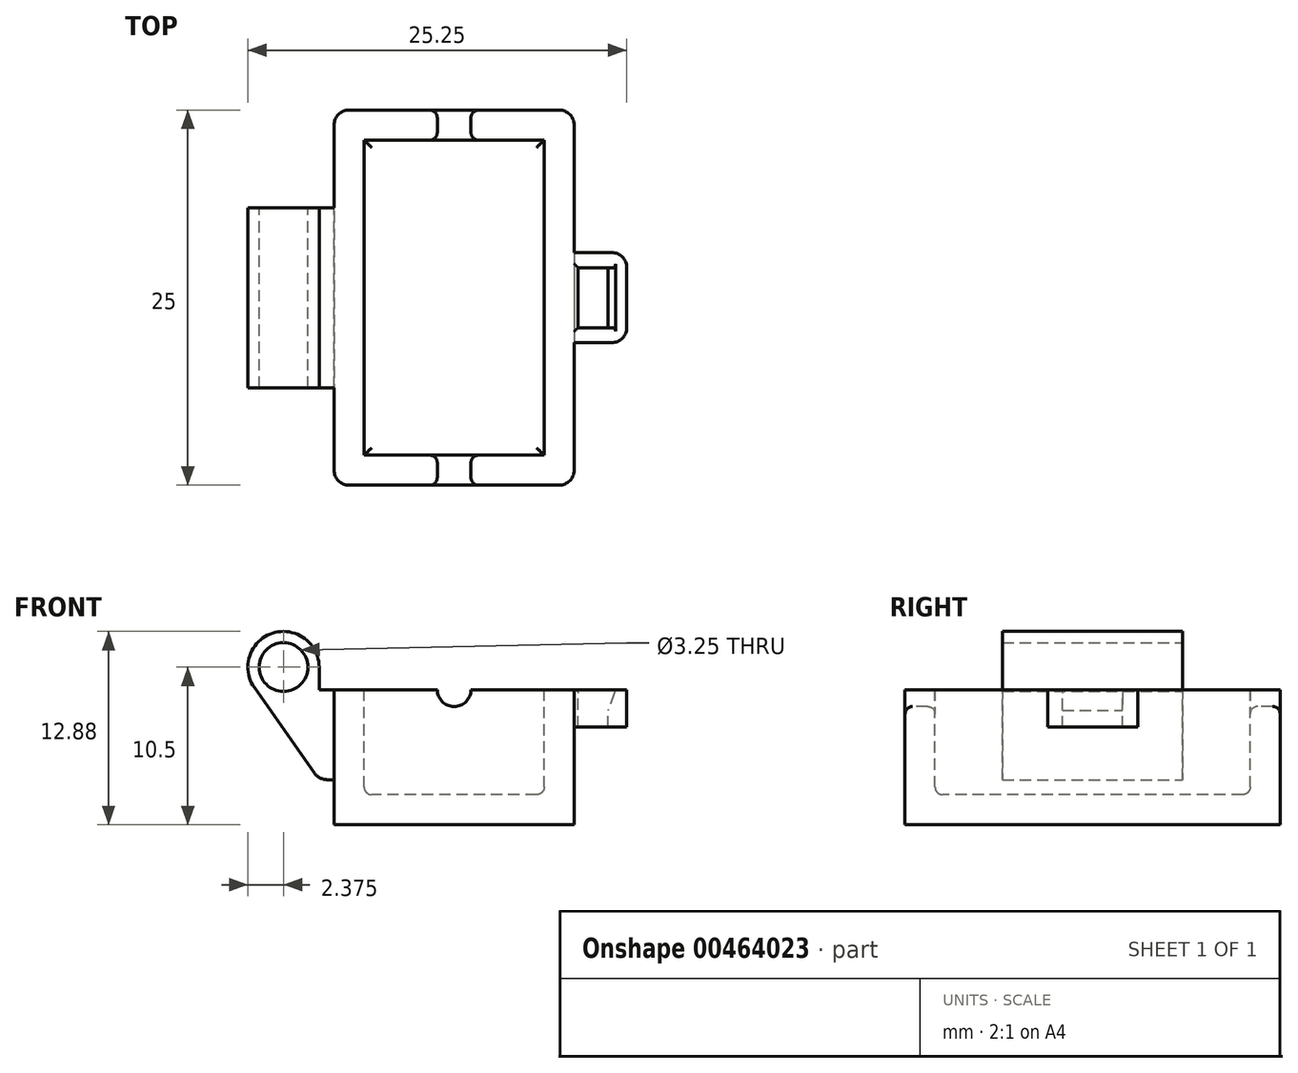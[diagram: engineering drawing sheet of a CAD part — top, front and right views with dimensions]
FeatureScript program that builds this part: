
annotation { "Feature Type Name" : "Feature", "Feature Type Description" : "" }
export const myFeature = defineFeature(function(context is Context, id is Id, definition is map)
    precondition{}
    {
        {
            var Q0;
            Q0=qCreatedBy(makeId("Top.planeOp"),FACE);
            var sketch = newSketch(context, id + "F0", { "sketchPlane" : qUnion([Q0])});
            skLineSegment(sketch, "E0.bottom", {"start": v(8, 12.5) * mm, "end": v(-8, 12.5) * mm});
            skLineSegment(sketch, "E0.top", {"start": v(8, -12.5) * mm, "end": v(-8, -12.5) * mm});
            skLineSegment(sketch, "E0.left", {"start": v(8, 12.5) * mm, "end": v(8, -12.5) * mm});
            skLineSegment(sketch, "E0.right", {"start": v(-8, 12.5) * mm, "end": v(-8, -12.5) * mm});
            skPoint(sketch, "E0.middle", {"position": v(0, 0) * mm});
            skSolve(sketch);
        }
        {
            var Q0;
            Q0 = qSketchRegion(id + "F0", true);
            extrude(context, id + "F1", {"entities" : qUnion([Q0]), "oppositeDirection" : true, "depth" : 9 * mm});
        }
        {
            var Q0;
            Q0=makeQuery(id+"F1.opExtrude","CAP_FACE",FACE,{"disambiguationData":[OSD([sQuery(id+"F0.wireOp",EDGE,"E0.bottom"),sQuery(id+"F0.wireOp",EDGE,"E0.top"),sQuery(id+"F0.wireOp",EDGE,"E0.left"),sQuery(id+"F0.wireOp",EDGE,"E0.right")])],"isStart":true});
            shell(context, id + "F2", {"entities" : qUnion([Q0]), "thickness" : 2 * mm});
        }
        {
            var Q0;
            Q0=qCreatedBy(makeId("Front.planeOp"),FACE);
            var sketch = newSketch(context, id + "F3", { "sketchPlane" : qUnion([Q0])});
            skLineSegment(sketch, "E1", {"start": v(-13.32, 0.13) * mm, "end": v(-9, -6) * mm});
            skArc(sketch, "E2", {"start": v(-9, 1.5) * mm, "mid": v(-12.1, 3.76) * mm, "end": v(-13.32, 0.13) * mm});
            skLineSegment(sketch, "E3", {"start": v(-9, 1.5) * mm, "end": v(-9, 0) * mm});
            skLineSegment(sketch, "E4", {"start": v(-9, 0) * mm, "end": v(-8, 0) * mm});
            skLineSegment(sketch, "E5.0", {"start": v(-8, -6) * mm, "end": v(-8, 0) * mm});
            skLineSegment(sketch, "E6", {"start": v(-9, -6) * mm, "end": v(-8, -6) * mm});
            skPoint(sketch, "E7.orphan", {"position": v(-8, -9) * mm});
            skSolve(sketch);
        }
        {
            var Q0;
            Q0 = qSketchRegion(id + "F3", true);
            extrude(context, id + "F4", {"entities" : qUnion([Q0]), "operationType" : NewBodyOperationType.ADD, "endBound" : BoundingType.SYMMETRIC, "depth" : 12 * mm});
        }
        {
            var Q0;
            Q0=makeQuery(id+"F4.opExtrude","CAP_FACE",FACE,{"disambiguationData":[OSD([sQuery(id+"F3.wireOp",EDGE,"uH9xqNTA-Io9C-N20J-ZzZ9-npMpiWseRlYH"),sQuery(id+"F3.wireOp",EDGE,"l0RrsI6B-aDfr-OfvM-JG3k-yMFCeRe5ejhv"),sQuery(id+"F3.wireOp",EDGE,"E1"),sQuery(id+"F3.wireOp",EDGE,"81e93450-e998-4614-a5fd-c4c0534a458d.0"),sQuery(id+"F3.wireOp",EDGE,"b74dccb4-ed0e-4af8-89a9-468f63bd8629.0")])],"isStart":true});
            var sketch = newSketch(context, id + "F5", { "sketchPlane" : qUnion([Q0])});
            skCircle(sketch, "E8", {"center": v(11.38, 1.5) * mm, "radius": 1.63 * mm});
            skSolve(sketch);
        }
        {
            var Q0;
            Q0 = qSketchRegion(id + "F5", true);
            extrude(context, id + "F6", {"entities" : qUnion([Q0]), "operationType" : NewBodyOperationType.REMOVE, "oppositeDirection" : true, "depth" : 25 * mm});
        }
        {
            var Q0;
            Q0=qCreatedBy(makeId("Front.planeOp"),FACE);
            var sketch = newSketch(context, id + "F7", { "sketchPlane" : qUnion([Q0])});
            skCircle(sketch, "E9", {"center": v(0, 0) * mm, "radius": 1.13 * mm});
            skSolve(sketch);
        }
        {
            var Q0;
            Q0 = qSketchRegion(id + "F7", true);
            extrude(context, id + "F8", {"entities" : qUnion([Q0]), "operationType" : NewBodyOperationType.REMOVE, "oppositeDirection" : true, "depth" : 25 * mm, "hasSecondDirection" : true, "secondDirectionOppositeDirection" : false, "secondDirectionDepth" : 25 * mm});
        }
        {
            var Q0;
            Q0=makeQuery(id+"F4.opExtrude","SWEPT_EDGE",EDGE,{"disambiguationData":[OSD([sQuery(id+"F3.wireOp",EDGE,"E1"),sQuery(id+"F3.wireOp",EDGE,"81e93450-e998-4614-a5fd-c4c0534a458d.0")])]});
            fillet(context, id + "F9", {"entities" : qUnion([Q0]), "radius" : 1 * mm, "tangentPropagation" : true, "allowEdgeOverflow" : false});
        }
        {
            var Q0;
            Q0=makeQuery(id+"F1.opExtrude","SWEPT_FACE",FACE,{"disambiguationData":[OSD([sQuery(id+"F0.wireOp",EDGE,"E0.left")])]});
            var sketch = newSketch(context, id + "F10", { "sketchPlane" : qUnion([Q0])});
            skLineSegment(sketch, "E10.bottom", {"start": v(1, -1.75) * mm, "end": v(-1, -1.75) * mm});
            skLineSegment(sketch, "E10.top", {"start": v(1, -0.75) * mm, "end": v(-1, -0.75) * mm});
            skLineSegment(sketch, "E10.left", {"start": v(1, -1.75) * mm, "end": v(1, -0.75) * mm});
            skLineSegment(sketch, "E10.right", {"start": v(-1, -1.75) * mm, "end": v(-1, -0.75) * mm});
            skPoint(sketch, "E10.middle", {"position": v(0, -1.25) * mm});
            skSolve(sketch);
        }
        {
            var Q0;
            {var subQ0=sQuery(id+"F0.wireOp",EDGE,"E0.left");var subQ1=sQuery(id+"F0.wireOp",EDGE,"E0.top");var subQ2=sQuery(id+"F0.wireOp",EDGE,"E0.bottom");Q0=makeQuery(id+"F8.boolean.opBoolean","SPLIT",FACE,{"disambiguationData":[TD([makeQuery(id+"F1.opExtrude","SWEPT_FACE",FACE,{"disambiguationData":[OSD([subQ0])]})])],"derivedFrom":makeQuery(id+"F1.opExtrude","CAP_FACE",FACE,{"disambiguationData":[OSD([subQ2,subQ1,subQ0,sQuery(id+"F0.wireOp",EDGE,"E0.right")])],"isStart":true})});}
            var sketch = newSketch(context, id + "F11", { "sketchPlane" : qUnion([Q0])});
            skLineSegment(sketch, "E11.bottom", {"start": v(8, 3) * mm, "end": v(11.5, 3) * mm});
            skLineSegment(sketch, "E11.top", {"start": v(8, -3) * mm, "end": v(11.5, -3) * mm});
            skLineSegment(sketch, "E11.left", {"start": v(8, 3) * mm, "end": v(8, -3) * mm});
            skLineSegment(sketch, "E11.right", {"start": v(11.5, 3) * mm, "end": v(11.5, -3) * mm});
            skLineSegment(sketch, "E12.bottom", {"start": v(8.25, 2) * mm, "end": v(10.25, 2) * mm});
            skLineSegment(sketch, "E12.top", {"start": v(8.25, -2) * mm, "end": v(10.25, -2) * mm});
            skLineSegment(sketch, "E12.left", {"start": v(8.25, 2) * mm, "end": v(8.25, -2) * mm});
            skLineSegment(sketch, "E12.right", {"start": v(10.25, 2) * mm, "end": v(10.25, -2) * mm});
            skSolve(sketch);
        }
        {
            var Q0;
            Q0 = qSketchRegion(id + "F11", true);
            extrude(context, id + "F12", {"entities" : qUnion([Q0]), "operationType" : NewBodyOperationType.ADD, "oppositeDirection" : true, "depth" : 2.5 * mm});
        }
        {
            var Q0;
            Q0=makeQuery(id+"F12.opExtrude","SWEPT_EDGE",EDGE,{"disambiguationData":[OSD([sQuery(id+"F11.wireOp",EDGE,"E11.top"),sQuery(id+"F11.wireOp",EDGE,"E11.right")])]});
            var Q1;
            Q1=makeQuery(id+"F12.opExtrude","SWEPT_EDGE",EDGE,{"disambiguationData":[OSD([sQuery(id+"F0.wireOp",EDGE,"E0.left"),sQuery(id+"F11.wireOp",EDGE,"E11.top"),sQuery(id+"F11.wireOp",EDGE,"E11.left")])]});
            var Q2;
            Q2=makeQuery(id+"F12.opExtrude","SWEPT_EDGE",EDGE,{"disambiguationData":[OSD([sQuery(id+"F11.wireOp",EDGE,"E11.bottom"),sQuery(id+"F11.wireOp",EDGE,"E11.right")])]});
            var Q3;
            Q3=makeQuery(id+"F12.opExtrude","SWEPT_EDGE",EDGE,{"disambiguationData":[OSD([sQuery(id+"F0.wireOp",EDGE,"E0.left"),sQuery(id+"F11.wireOp",EDGE,"E11.bottom"),sQuery(id+"F11.wireOp",EDGE,"E11.left")])]});
            fillet(context, id + "F13", {"entities" : qUnion([Q0, Q1, Q2, Q3]), "radius" : 1 * mm, "tangentPropagation" : true, "allowEdgeOverflow" : false});
        }
        {
            var Q0;
            Q0=makeQuery(id+"F12.opExtrude","CAP_EDGE",EDGE,{"disambiguationData":[OSD([sQuery(id+"F11.wireOp",EDGE,"E12.bottom")])],"isStart":true});
            var Q1;
            Q1=makeQuery(id+"F12.opExtrude","CAP_EDGE",EDGE,{"disambiguationData":[OSD([sQuery(id+"F11.wireOp",EDGE,"E12.left")])],"isStart":true});
            var Q2;
            Q2=makeQuery(id+"F12.opExtrude","CAP_EDGE",EDGE,{"disambiguationData":[OSD([sQuery(id+"F11.wireOp",EDGE,"E12.top")])],"isStart":true});
            fillet(context, id + "F14", {"entities" : qUnion([Q0, Q1, Q2]), "radius" : .25 * mm, "tangentPropagation" : true, "allowEdgeOverflow" : false});
        }
        {
            var Q0;
            Q0=makeQuery(id+"F12.opExtrude","CAP_EDGE",EDGE,{"disambiguationData":[OSD([sQuery(id+"F11.wireOp",EDGE,"E12.right")])],"isStart":true});
            chamfer(context, id + "F15", {"entities" : qUnion([Q0]), "chamferType" : ChamferType.OFFSET_ANGLE, "width" : .5 * mm, "oppositeDirection" : false, "angle" : 70 * degree, "tangentPropagation" : true});
        }
        {
            var Q0;
            Q0=makeQuery(id+"F8.boolean.opBoolean","INTERSECT",EDGE,{"derivedFrom":[makeQuery(id+"F1.opExtrude","SWEPT_FACE",FACE,{"disambiguationData":[OSD([sQuery(id+"F0.wireOp",EDGE,"E0.bottom")])]}),makeQuery(id+"F8.opExtrude","SWEPT_FACE",FACE,{"disambiguationData":[OSD([sQuery(id+"F7.wireOp",EDGE,"E9")])]})]});
            var Q1;
            Q1=makeQuery(id+"F8.boolean.opBoolean","INTERSECT",EDGE,{"derivedFrom":[makeQuery(id+"F1.opExtrude","SWEPT_FACE",FACE,{"disambiguationData":[OSD([sQuery(id+"F0.wireOp",EDGE,"E0.top")])]}),makeQuery(id+"F8.opExtrude","SWEPT_FACE",FACE,{"disambiguationData":[OSD([sQuery(id+"F7.wireOp",EDGE,"E9")])]})]});
            fillet(context, id + "F16", {"entities" : qUnion([Q0, Q1]), "radius" : .5 * mm, "tangentPropagation" : true, "allowEdgeOverflow" : false});
        }
        {
            var Q0;
            Q0=makeQuery(id+"F8.boolean.opBoolean","INTERSECT",EDGE,{"derivedFrom":[makeQuery(id+"F2.opShell","OFFSET_FACE",FACE,{"disambiguationData":[OSD([sQuery(id+"F0.wireOp",EDGE,"E0.bottom")])]}),makeQuery(id+"F8.opExtrude","SWEPT_FACE",FACE,{"disambiguationData":[OSD([sQuery(id+"F7.wireOp",EDGE,"E9")])]})]});
            var Q1;
            {var subQ0=sQuery(id+"F0.wireOp",EDGE,"E0.bottom");Q1=makeQuery(id+"F2.opShell","OFFSET_EDGE",EDGE,{"disambiguationData":[OSD([subQ0]),TDD([makeQuery(id+"F1.opExtrude","CAP_EDGE",EDGE,{"disambiguationData":[OSD([subQ0])],"isStart":false})])]});}
            var Q2;
            {var subQ0=sQuery(id+"F0.wireOp",EDGE,"E0.top");Q2=makeQuery(id+"F2.opShell","OFFSET_EDGE",EDGE,{"disambiguationData":[OSD([subQ0]),TDD([makeQuery(id+"F1.opExtrude","CAP_EDGE",EDGE,{"disambiguationData":[OSD([subQ0])],"isStart":false})])]});}
            var Q3;
            {var subQ0=sQuery(id+"F0.wireOp",EDGE,"E0.left");Q3=makeQuery(id+"F2.opShell","OFFSET_EDGE",EDGE,{"disambiguationData":[OSD([subQ0]),TDD([makeQuery(id+"F1.opExtrude","CAP_EDGE",EDGE,{"disambiguationData":[OSD([subQ0])],"isStart":false})])]});}
            var Q4;
            Q4=makeQuery(id+"F8.boolean.opBoolean","INTERSECT",EDGE,{"derivedFrom":[makeQuery(id+"F2.opShell","OFFSET_FACE",FACE,{"disambiguationData":[OSD([sQuery(id+"F0.wireOp",EDGE,"E0.top")])]}),makeQuery(id+"F8.opExtrude","SWEPT_FACE",FACE,{"disambiguationData":[OSD([sQuery(id+"F7.wireOp",EDGE,"E9")])]})]});
            var Q5;
            {var subQ0=sQuery(id+"F0.wireOp",EDGE,"E0.right");Q5=makeQuery(id+"F2.opShell","OFFSET_EDGE",EDGE,{"disambiguationData":[OSD([subQ0]),TDD([makeQuery(id+"F1.opExtrude","CAP_EDGE",EDGE,{"disambiguationData":[OSD([subQ0])],"isStart":false})])]});}
            fillet(context, id + "F17", {"entities" : qUnion([Q0, Q1, Q2, Q3, Q4, Q5]), "radius" : .5 * mm, "tangentPropagation" : true, "allowEdgeOverflow" : false});
        }
        {
            var Q0;
            Q0=makeQuery(id+"F1.opExtrude","SWEPT_EDGE",EDGE,{"disambiguationData":[OSD([sQuery(id+"F0.wireOp",EDGE,"E0.bottom"),sQuery(id+"F0.wireOp",EDGE,"E0.left")])]});
            var Q1;
            Q1=makeQuery(id+"F1.opExtrude","SWEPT_EDGE",EDGE,{"disambiguationData":[OSD([sQuery(id+"F0.wireOp",EDGE,"E0.bottom"),sQuery(id+"F0.wireOp",EDGE,"E0.right")])]});
            var Q2;
            Q2=makeQuery(id+"F1.opExtrude","SWEPT_EDGE",EDGE,{"disambiguationData":[OSD([sQuery(id+"F0.wireOp",EDGE,"E0.top"),sQuery(id+"F0.wireOp",EDGE,"E0.left")])]});
            var Q3;
            Q3=makeQuery(id+"F1.opExtrude","SWEPT_EDGE",EDGE,{"disambiguationData":[OSD([sQuery(id+"F0.wireOp",EDGE,"E0.top"),sQuery(id+"F0.wireOp",EDGE,"E0.right")])]});
            fillet(context, id + "F18", {"entities" : qUnion([Q0, Q1, Q2, Q3]), "radius" : 1 * mm, "tangentPropagation" : true, "allowEdgeOverflow" : false});
        }
    });
